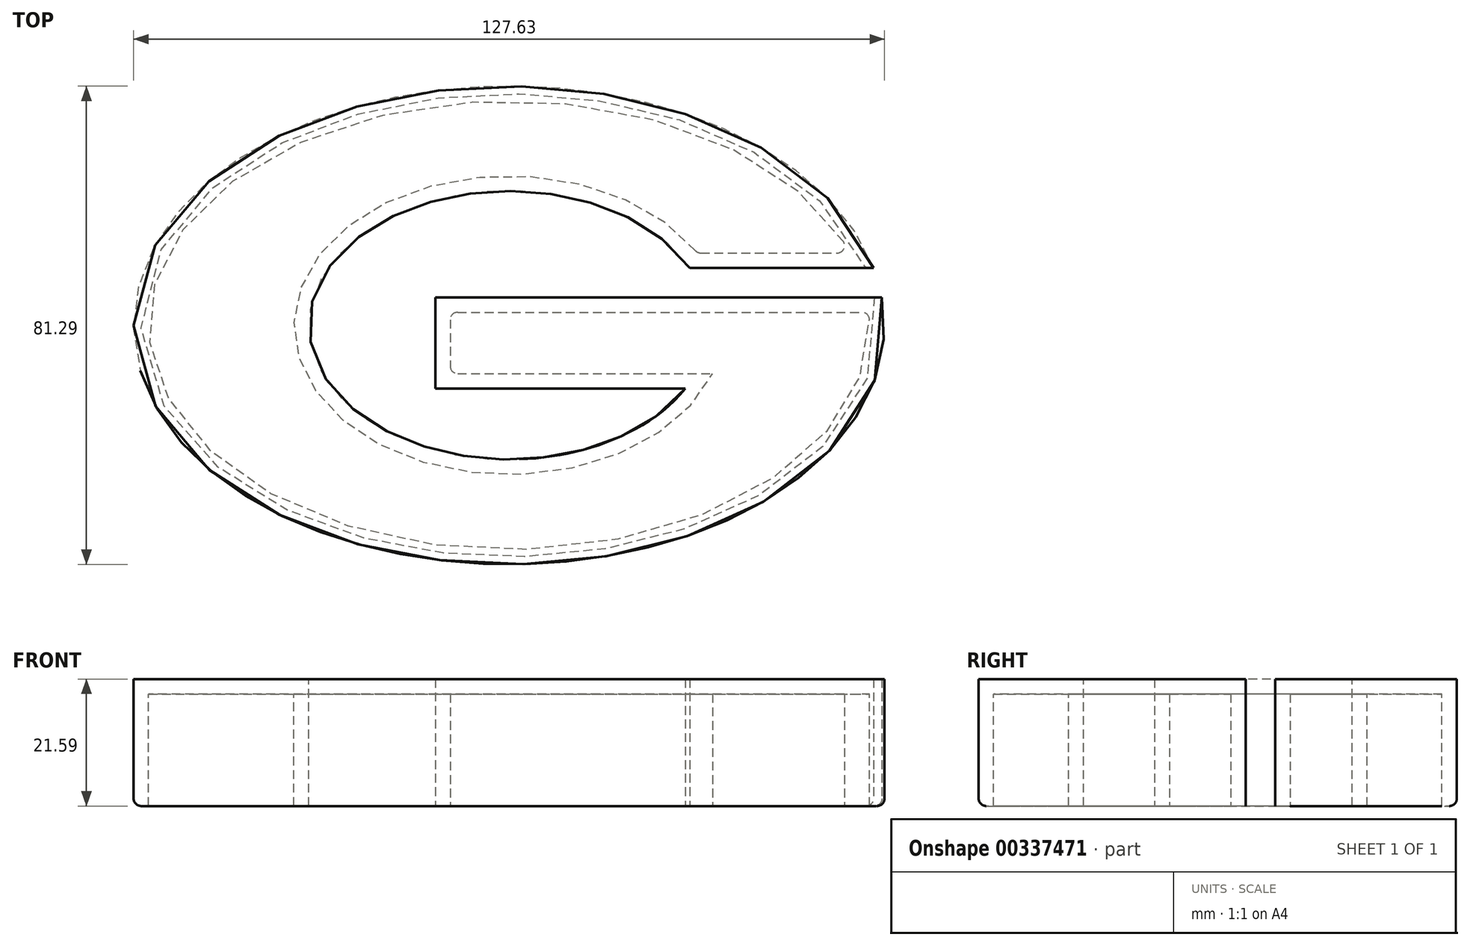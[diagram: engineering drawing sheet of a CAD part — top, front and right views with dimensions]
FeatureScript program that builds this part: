
annotation { "Feature Type Name" : "Feature", "Feature Type Description" : "" }
export const myFeature = defineFeature(function(context is Context, id is Id, definition is map)
    precondition{}
    {
        {
            var Q0;
            Q0=qCreatedBy(makeId("Top.planeOp"),FACE);
            var sketch = newSketch(context, id + "F0", { "sketchPlane" : qUnion([Q0])});
            skPoint(sketch, "E0.0.internal.snap0", {"position": v(-62.27, -2.26) * mm});
            skLineSegment(sketch, "E1", {"start": v(0, 0) * mm, "end": v(71.18, 0) * mm});
            skEllipticalArc(sketch, "E2", {});
            skEllipticalArc(sketch, "E3", {});
            skLineSegment(sketch, "E4", {"start": v(42, 10.1) * mm, "end": v(68, 10.1) * mm});
            skLineSegment(sketch, "E5", {"start": v(0, 0) * mm, "end": v(0, -10.41) * mm});
            skLineSegment(sketch, "E6", {"start": v(0, -10.41) * mm, "end": v(44.6, -10.41) * mm});
            const initialGuessF0  = {"E2": [0.01000629193665377, -0.0021947082449912648, -1, 0, 0.06127366874342576, 0.0381, 3.4699594231751796, 3.1992284491482423], "E3": [0.01000629193665377, -0.0021947082449912648, -1, 0, 0.0365687312801792, 0.025360236479678888, 3.6473895686891957, 2.811690888425089]};
            skSetInitialGuess(sketch, initialGuessF0);
            skSolve(sketch);
        }
        {
            var Q0;
            Q0=makeQuery(id+"F0.imprint","IMPRINT",FACE,{"disambiguationData":[TD([[makeQuery(id+"F0.imprint","IMPRINT",EDGE,{"derivedFrom":sQuery(id+"F0.wireOp",EDGE,"E2")}),1.0]])]});
            extrude(context, id + "F1", {"entities" : qUnion([Q0]), "depth" : 19.05 * mm});
        }
        {
            var Q0;
            Q0=makeQuery(id+"F1.opExtrude","CAP_FACE",FACE,{"disambiguationData":[OSD([sQuery(id+"F0.wireOp",EDGE,"E2"),sQuery(id+"F0.wireOp",EDGE,"E3"),sQuery(id+"F0.wireOp",EDGE,"E4"),sQuery(id+"F0.wireOp",EDGE,"E1"),sQuery(id+"F0.wireOp",EDGE,"E5"),sQuery(id+"F0.wireOp",EDGE,"E6")])],"isStart":true});
            shell(context, id + "F2", {"entities" : qUnion([Q0]), "thickness" : 2.54 * mm, "oppositeDirection" : true});
        }
        {
            var Q0;
            Q0=makeQuery(id+"F1.opExtrude","CAP_EDGE",EDGE,{"disambiguationData":[OSD([sQuery(id+"F0.wireOp",EDGE,"E2")])],"isStart":true});
            fillet(context, id + "F3", {"entities" : qUnion([Q0]), "radius" : 1.27 * mm, "tangentPropagation" : true, "allowEdgeOverflow" : false});
        }
        {
            var Q0;
            Q0=makeQuery(id+"F2.opShell","OFFSET_EDGE",EDGE,{"disambiguationData":[OSD([sQuery(id+"F0.wireOp",EDGE,"E2"),sQuery(id+"F0.wireOp",EDGE,"E1")])]});
            var Q1;
            Q1=makeQuery(id+"F2.opShell","OFFSET_EDGE",EDGE,{"disambiguationData":[OSD([sQuery(id+"F0.wireOp",EDGE,"E2"),sQuery(id+"F0.wireOp",EDGE,"E4")])]});
            var Q2;
            Q2=makeQuery(id+"F2.opShell","OFFSET_EDGE",EDGE,{"disambiguationData":[OSD([sQuery(id+"F0.wireOp",EDGE,"E1"),sQuery(id+"F0.wireOp",EDGE,"E5")])]});
            var Q3;
            Q3=makeQuery(id+"F2.opShell","OFFSET_EDGE",EDGE,{"disambiguationData":[OSD([sQuery(id+"F0.wireOp",EDGE,"E5"),sQuery(id+"F0.wireOp",EDGE,"E6")])]});
            fillet(context, id + "F4", {"entities" : qUnion([Q0, Q1, Q2, Q3]), "radius" : 1.27 * mm, "tangentPropagation" : true, "allowEdgeOverflow" : false});
        }
        {
            var Q0;
            Q0=makeQuery(id+"F2.opShell","OFFSET_EDGE",EDGE,{"disambiguationData":[OSD([sQuery(id+"F0.wireOp",EDGE,"E3"),sQuery(id+"F0.wireOp",EDGE,"E4")])]});
            fillet(context, id + "F5", {"entities" : qUnion([Q0]), "radius" : 1.27 * mm, "tangentPropagation" : true, "allowEdgeOverflow" : false});
        }
    });
